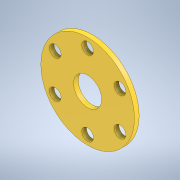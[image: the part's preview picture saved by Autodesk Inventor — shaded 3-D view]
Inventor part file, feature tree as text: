
AUTODESK INVENTOR PART (.ipt)
format: ipt  version: 2020 (Build 240168000, 168)  size: 131,072 bytes
history: native  units: mm
features: sketch x2, revolve x1, hole x1, pattern_circular x1
ambient origin geometry x8: Origin, YZ Plane, XZ Plane, XY Plane, X Axis, Y Axis, Z Axis, Center Point
bodies: Solid1 (feature_tree)
feature tree (5):
  revolve  "Revolution1"  [1 undecoded]
  hole  "Hole1"  [1 undecoded]
  pattern_circular  "Circular Pattern1"  Count=6 Angle=360.0deg
  sketch  "Sketch1"  dims[d3=2.0mm d4=40.0mm]
  sketch  "Sketch2"  dims[d5=90.0deg d6=16.0mm d7=5.0mm d8=6.0mm d9=4.0mm d10=2.0mm d11=90.0deg d12=8.0mm d13=20.594885mm d14=60.0mm d15=360.0deg d28=12.0mm]
note: 2 required parameter values undecoded (feature->parameter linkage not recoverable at this tier; creation-order binding heuristic only, values carry confidence <= 0.55)